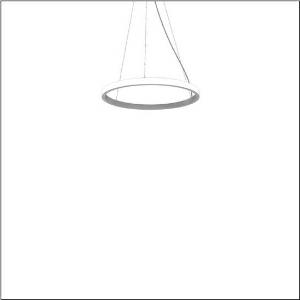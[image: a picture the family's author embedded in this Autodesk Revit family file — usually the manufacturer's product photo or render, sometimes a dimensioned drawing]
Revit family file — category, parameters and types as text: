
# Revit family: silica_21_ring-o_5pjbo1d1204a
name_source: partatom
category: Lighting Fixtures
units: mm (PartAtom-declared; Revit-internal decimal feet)

## family parameters
Cut with Voids When Loaded = No
Host = Face
Light Source = No
Part Type = Normal
Room Calculation Point = No
Round Connector Dimension = Use Diameter
Shared = No

## types (1)
- Silica 21 Ring-O (1 x LED, 3740 lm, 60 W, 3000K)
    Apparent Load = 60 VA
    CIE Flux Codes = 2 16 49 50 100
    Color Rendering = 80
    Color Temperature = 3000K
    Default Elevation = 1800 mm
    Description = Silica 21 Ring-O, suspended luminaire, of PMMA, frosted, light emission: outer ring side luminous distribution, primary light characteristic: symmetric, installation type: suspended mounting, LED, rated luminous flux: 3.744lm, luminous efficacy: 62lm/W, light colour: 830, colour temperature: 3000K, control gear: DALI 2, with terminal, 5-pole, mains connection: 230V, AC/DC, 0/50..60Hz, rated input power: 60W, housing, of extruded aluminium section, metallic grey (RAL 9006), diameter: 610mm, ceiling canopy, metallic grey (RAL 9006), protection rating (lamp compartment): IP40, insulation class (complete): insulation class I (protective earthing), certification: CE, impact resistance: IK02, permissible operating ambient temperature: 0..+35°C, packaging unit: 1 piece
    Height = 48 mm  [stored 0.15748 ft]
    Lamp = 1 x LED
    Lamp Light Flux = 3740 lm
    Lamp Power = 60 W
    Lamp count = 1
    Length = 610 mm
    Luminous efficacy = 62 lm/W
    Manufacturer = Siteco
    ModVariant = No
    Model = 5PJBO1D1204A
    Mounting Place = Ceiling
    Mounting Type = Pendant
    Number of Poles = 1
    OnlyDefault = Yes
    Power Factor = 1
    Product Name = Silica 21 Ring-O
    Product group = suspended luminaire
    ProductGroupID = 904
    Protection Class = Protection class I
    Protection Degree = IP 40
    RLX_Detail_Level = 1
    RLX_Emergency_Light_Flux = 0 lm
    RLX_Emergency_Type = 0
    RLX_Emergency_Type_DB = No
    RlxData = <blob elided: 11609 chars, md5=3939cc36>
    Socket = socket
    Standby Power = 0 W
    System Light Flux = 3740 lm
    System Power = 60 W
    Type Comments = Product without accessories
    Type Image = l_1251758.jpg
    URL = http://relux.com
    VarID = ---
    Voltage = 0 V
    Weight = 0.00 kg
    Width = 0 mm  [stored 0 ft]

note: [stored X ft] marks values corroborated as IEEE doubles in the binary element streams (Revit-internal decimal feet)

## geometry (parser evidence)
native form markers: Sweep x12
no freeform markers — native parametric forms only
